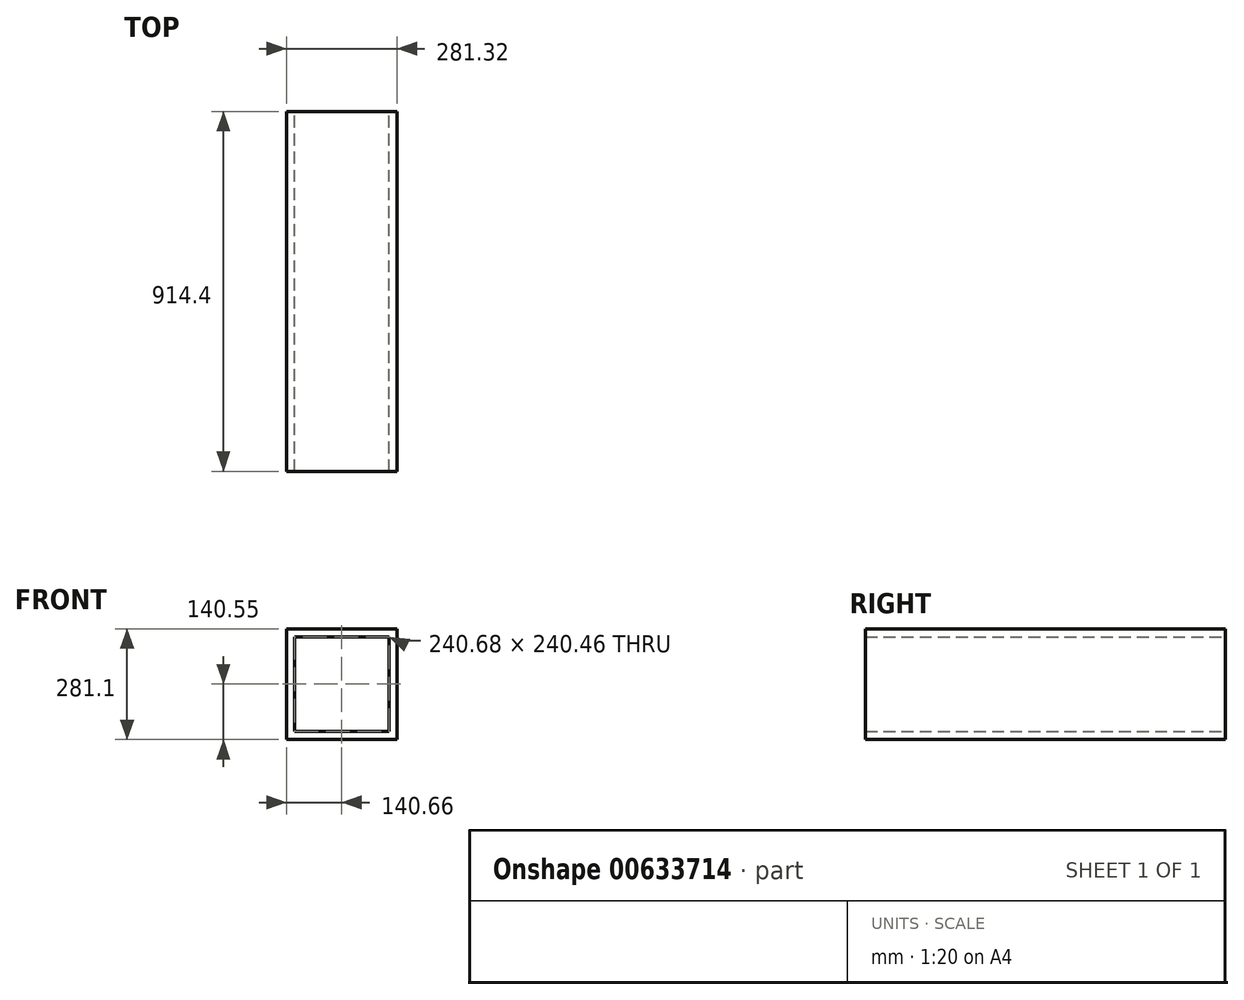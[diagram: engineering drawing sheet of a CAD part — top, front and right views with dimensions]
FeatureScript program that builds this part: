
annotation { "Feature Type Name" : "Feature", "Feature Type Description" : "" }
export const myFeature = defineFeature(function(context is Context, id is Id, definition is map)
    precondition{}
    {
        {
            var Q0;
            Q0=qCreatedBy(makeId("Front.planeOp"),FACE);
            var sketch = newSketch(context, id + "F0", { "sketchPlane" : qUnion([Q0])});
            skLineSegment(sketch, "E0.bottom", {"start": v(-140.66, 140.55) * mm, "end": v(140.66, 140.55) * mm});
            skLineSegment(sketch, "E0.top", {"start": v(-140.66, -140.55) * mm, "end": v(140.66, -140.55) * mm});
            skLineSegment(sketch, "E0.left", {"start": v(-140.66, 140.55) * mm, "end": v(-140.66, -140.55) * mm});
            skLineSegment(sketch, "E0.right", {"start": v(140.66, 140.55) * mm, "end": v(140.66, -140.55) * mm});
            skPoint(sketch, "E0.middle", {"position": v(0, 0) * mm});
            skSolve(sketch);
        }
        {
            var Q0;
            Q0 = qSketchRegion(id + "F0", true);
            extrude(context, id + "F1", {"entities" : qUnion([Q0]), "depth" : 914.4 * mm, "offsetDistance" : 25.4 * mm});
        }
        {
            var Q0;
            Q0=makeQuery(id+"F1.opExtrude","CAP_FACE",FACE,{"disambiguationData":[OSD([sQuery(id+"F0.wireOp",EDGE,"E0.bottom"),sQuery(id+"F0.wireOp",EDGE,"E0.top"),sQuery(id+"F0.wireOp",EDGE,"E0.left"),sQuery(id+"F0.wireOp",EDGE,"E0.right")])],"isStart":false});
            var Q1;
            Q1=makeQuery(id+"F1.opExtrude","CAP_FACE",FACE,{"disambiguationData":[OSD([sQuery(id+"F0.wireOp",EDGE,"E0.bottom"),sQuery(id+"F0.wireOp",EDGE,"E0.top"),sQuery(id+"F0.wireOp",EDGE,"E0.left"),sQuery(id+"F0.wireOp",EDGE,"E0.right")])],"isStart":true});
            shell(context, id + "F2", {"entities" : qUnion([Q0, Q1]), "thickness" : 20.32 * mm});
        }
    });
